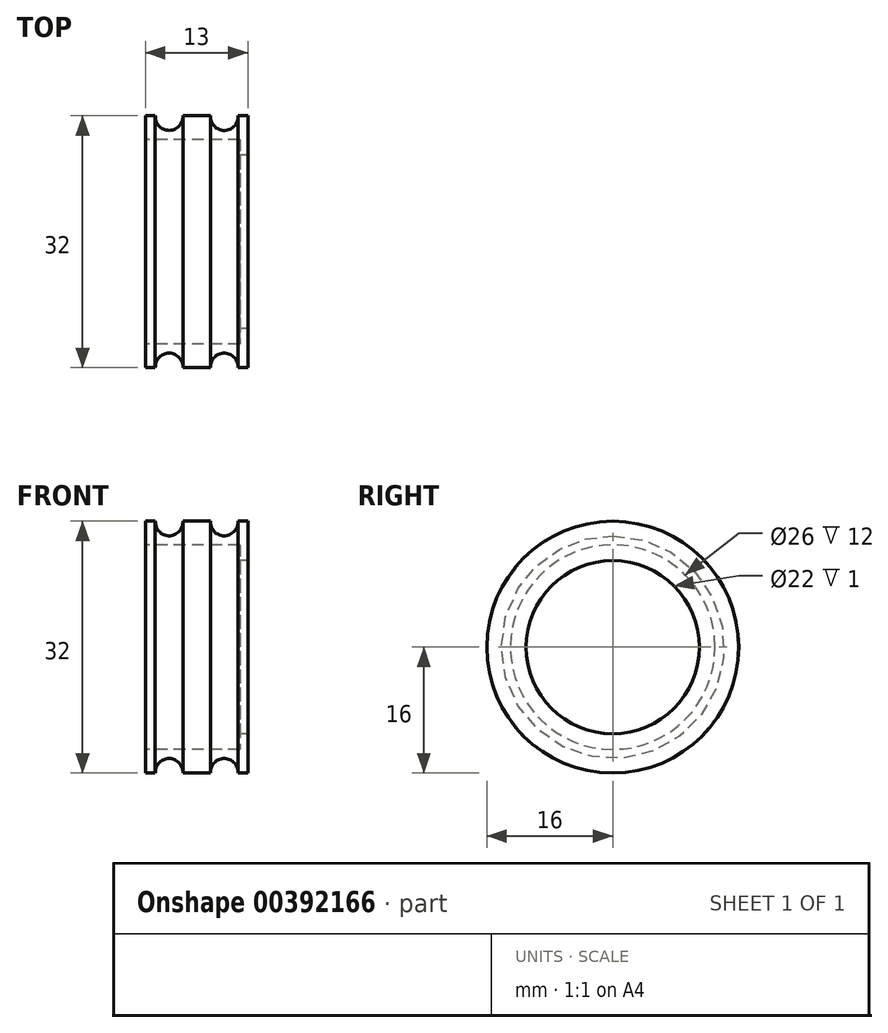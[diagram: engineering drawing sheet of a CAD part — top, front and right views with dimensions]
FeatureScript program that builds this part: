
annotation { "Feature Type Name" : "Feature", "Feature Type Description" : "" }
export const myFeature = defineFeature(function(context is Context, id is Id, definition is map)
    precondition{}
    {
        {
            var Q0;
            Q0=qCreatedBy(makeId("Front.planeOp"),FACE);
            var sketch = newSketch(context, id + "F0", { "sketchPlane" : qUnion([Q0])});
            skLineSegment(sketch, "E0", {"start": v(0, 16) * mm, "end": v(1.25, 16) * mm});
            skLineSegment(sketch, "E1", {"start": v(12, 13) * mm, "end": v(0, 13) * mm});
            skLineSegment(sketch, "E2", {"start": v(0, 16) * mm, "end": v(0, 13) * mm});
            skLineSegment(sketch, "E3", {"start": v(12, 16) * mm, "end": v(13, 16) * mm});
            skLineSegment(sketch, "E4", {"start": v(13, 16) * mm, "end": v(13, 11) * mm});
            skLineSegment(sketch, "E5", {"start": v(13, 11) * mm, "end": v(12, 11) * mm});
            skLineSegment(sketch, "E6", {"start": v(12, 11) * mm, "end": v(12, 13) * mm});
            skArc(sketch, "E7", {"start": v(1.25, 15.86) * mm, "mid": v(3.02, 14.15) * mm, "end": v(4.75, 15.9) * mm});
            skArc(sketch, "E8", {"start": v(8.25, 15.92) * mm, "mid": v(10, 14.15) * mm, "end": v(11.75, 15.93) * mm});
            skLineSegment(sketch, "E9", {"start": v(4.75, 15.9) * mm, "end": v(4.75, 16) * mm});
            skLineSegment(sketch, "E10", {"start": v(1.25, 15.86) * mm, "end": v(1.25, 16) * mm});
            skLineSegment(sketch, "E11", {"start": v(8.25, 15.92) * mm, "end": v(8.25, 16) * mm});
            skLineSegment(sketch, "E12", {"start": v(11.75, 15.87) * mm, "end": v(11.75, 16) * mm});
            skLineSegment(sketch, "E13.trimOffspring", {"start": v(4.75, 16) * mm, "end": v(8.25, 16) * mm});
            skLineSegment(sketch, "E14.trimOffspring", {"start": v(11.75, 16) * mm, "end": v(12, 16) * mm});
            skLineSegment(sketch, "E15", {"start": v(0, 0) * mm, "end": v(17.52, 0) * mm});
            skSolve(sketch);
        }
        {
            var Q0;
            Q0=makeQuery(id+"F0.imprint","IMPRINT",FACE,{"disambiguationData":[TD([[makeQuery(id+"F0.imprint","IMPRINT",EDGE,{"derivedFrom":sQuery(id+"F0.wireOp",EDGE,"E0")}),-1.0]])]});
            var Q1;
            Q1=sQuery(id+"F0.wireOp",EDGE,"E15");
            revolve(context, id + "F1", {"entities" : qUnion([Q0]), "axis" : qUnion([Q1]), "revolveType" : RevolveType.FULL});
        }
    });
